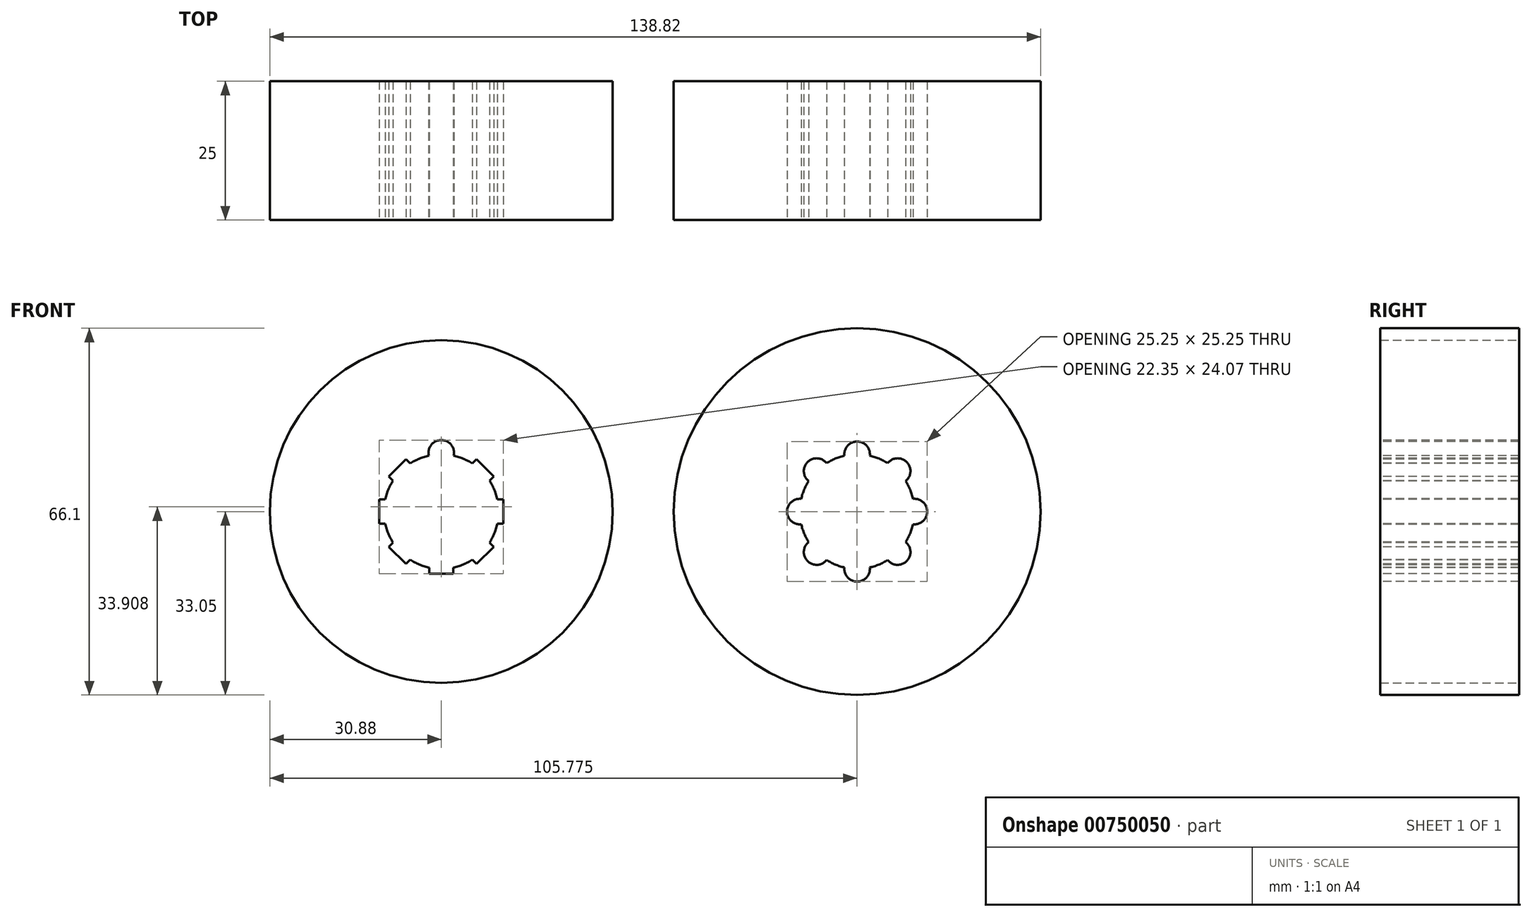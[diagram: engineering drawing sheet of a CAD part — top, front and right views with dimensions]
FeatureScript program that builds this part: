
annotation { "Feature Type Name" : "Feature", "Feature Type Description" : "" }
export const myFeature = defineFeature(function(context is Context, id is Id, definition is map)
    precondition{}
    {
        {
            var Q0;
            Q0=qCreatedBy(makeId("Front.planeOp"),FACE);
            var sketch = newSketch(context, id + "F0", { "sketchPlane" : qUnion([Q0])});
            skCircle(sketch, "E0", {"center": v(0, 0) * mm, "radius": 30.88 * mm});
            skSolve(sketch);
        }
        {
            var Q0;
            Q0 = qSketchRegion(id + "F0", true);
            extrude(context, id + "F1", {"entities" : qUnion([Q0]), "depth" : 25 * mm, "offsetDistance" : 25 * mm});
        }
        {
            var Q0;
            Q0=makeQuery(id+"F1.opExtrude","CAP_FACE",FACE,{"disambiguationData":[OSD([sQuery(id+"F0.wireOp",EDGE,"E0")])],"isStart":false});
            var sketch = newSketch(context, id + "F2", { "sketchPlane" : qUnion([Q0])});
            skCircle(sketch, "E1", {"center": v(0, 0) * mm, "radius": 11.18 * mm, "construction": true});
            skArc(sketch, "E2", {"start": v(-8.68, 5.6) * mm, "mid": v(-9.54, 3.95) * mm, "end": v(-10.1, 2.18) * mm});
            skLineSegment(sketch, "E3", {"start": v(0, 0) * mm, "end": v(0, 21.23) * mm, "construction": true});
            skLineSegment(sketch, "E4", {"start": v(0, 11.18) * mm, "end": v(2.18, 11.18) * mm, "construction": true});
            skLineSegment(sketch, "E5", {"start": v(2.18, 11.18) * mm, "end": v(-2.18, 11.18) * mm});
            skLineSegment(sketch, "E6", {"start": v(-2.18, 11.18) * mm, "end": v(-2.18, 10.1) * mm});
            skLineSegment(sketch, "E7", {"start": v(2.18, 11.18) * mm, "end": v(2.18, 10.1) * mm});
            skLineSegment(sketch, "E8.1.0", {"start": v(-9.44, 6.36) * mm, "end": v(-8.68, 5.6) * mm});
            skLineSegment(sketch, "E8.1.1", {"start": v(-6.36, 9.44) * mm, "end": v(-9.44, 6.36) * mm});
            skLineSegment(sketch, "E8.1.2", {"start": v(-6.36, 9.44) * mm, "end": v(-5.6, 8.68) * mm});
            skLineSegment(sketch, "E8.2.0", {"start": v(-11.18, -2.18) * mm, "end": v(-10.1, -2.18) * mm});
            skLineSegment(sketch, "E8.2.1", {"start": v(-11.18, 2.18) * mm, "end": v(-11.18, -2.18) * mm});
            skLineSegment(sketch, "E8.2.2", {"start": v(-11.18, 2.18) * mm, "end": v(-10.1, 2.18) * mm});
            skLineSegment(sketch, "E8.3.0", {"start": v(-6.36, -9.44) * mm, "end": v(-5.6, -8.68) * mm});
            skLineSegment(sketch, "E8.3.1", {"start": v(-9.44, -6.36) * mm, "end": v(-6.36, -9.44) * mm});
            skLineSegment(sketch, "E8.3.2", {"start": v(-9.44, -6.36) * mm, "end": v(-8.68, -5.6) * mm});
            skLineSegment(sketch, "E8.4.0", {"start": v(2.18, -11.18) * mm, "end": v(2.18, -10.1) * mm});
            skLineSegment(sketch, "E8.4.1", {"start": v(-2.18, -11.18) * mm, "end": v(2.18, -11.18) * mm});
            skLineSegment(sketch, "E8.4.2", {"start": v(-2.18, -11.18) * mm, "end": v(-2.18, -10.1) * mm});
            skLineSegment(sketch, "E8.5.0", {"start": v(9.44, -6.36) * mm, "end": v(8.68, -5.6) * mm});
            skLineSegment(sketch, "E8.5.1", {"start": v(6.36, -9.44) * mm, "end": v(9.44, -6.36) * mm});
            skLineSegment(sketch, "E8.5.2", {"start": v(6.36, -9.44) * mm, "end": v(5.6, -8.68) * mm});
            skLineSegment(sketch, "E8.6.0", {"start": v(11.18, 2.18) * mm, "end": v(10.1, 2.18) * mm});
            skLineSegment(sketch, "E8.6.1", {"start": v(11.18, -2.18) * mm, "end": v(11.18, 2.18) * mm});
            skLineSegment(sketch, "E8.6.2", {"start": v(11.18, -2.18) * mm, "end": v(10.1, -2.18) * mm});
            skLineSegment(sketch, "E8.7.0", {"start": v(6.36, 9.44) * mm, "end": v(5.6, 8.68) * mm});
            skLineSegment(sketch, "E8.7.1", {"start": v(9.44, 6.36) * mm, "end": v(6.36, 9.44) * mm});
            skLineSegment(sketch, "E8.7.2", {"start": v(9.44, 6.36) * mm, "end": v(8.68, 5.6) * mm});
            skArc(sketch, "E9.trimOffspring", {"start": v(-2.18, 10.1) * mm, "mid": v(-3.95, 9.54) * mm, "end": v(-5.6, 8.68) * mm});
            skArc(sketch, "E10.trimOffspring", {"start": v(5.6, 8.68) * mm, "mid": v(3.95, 9.54) * mm, "end": v(2.18, 10.1) * mm});
            skArc(sketch, "E11.trimOffspring", {"start": v(10.1, 2.18) * mm, "mid": v(9.54, 3.95) * mm, "end": v(8.68, 5.6) * mm});
            skArc(sketch, "E12.trimOffspring", {"start": v(8.68, -5.6) * mm, "mid": v(9.54, -3.95) * mm, "end": v(10.1, -2.18) * mm});
            skArc(sketch, "E13.trimOffspring", {"start": v(2.18, -10.1) * mm, "mid": v(3.95, -9.54) * mm, "end": v(5.6, -8.68) * mm});
            skArc(sketch, "E14.trimOffspring", {"start": v(-5.6, -8.68) * mm, "mid": v(-3.95, -9.54) * mm, "end": v(-2.18, -10.1) * mm});
            skArc(sketch, "E15.trimOffspring", {"start": v(-10.1, -2.18) * mm, "mid": v(-9.54, -3.95) * mm, "end": v(-8.68, -5.6) * mm});
            skSolve(sketch);
        }
        {
            var Q0;
            Q0 = qSketchRegion(id + "F2", true);
            extrude(context, id + "F3", {"entities" : qUnion([Q0]), "operationType" : NewBodyOperationType.REMOVE, "oppositeDirection" : true, "depth" : 25 * mm, "offsetDistance" : 25 * mm});
        }
        {
            var Q0;
            Q0=makeQuery(id+"F1.opExtrude","CAP_FACE",FACE,{"disambiguationData":[OSD([sQuery(id+"F0.wireOp",EDGE,"E0")])],"isStart":false});
            var sketch = newSketch(context, id + "F4", { "sketchPlane" : qUnion([Q0])});
            skCircle(sketch, "E16", {"center": v(0, 10.6) * mm, "radius": 2.3 * mm});
            skCircle(sketch, "E17", {"center": v(0, 0) * mm, "radius": 10.6 * mm, "construction": true});
            skSolve(sketch);
        }
        {
            var Q0;
            Q0 = qSketchRegion(id + "F4", true);
            extrude(context, id + "F5", {"entities" : qUnion([Q0]), "operationType" : NewBodyOperationType.REMOVE, "oppositeDirection" : true, "depth" : 25 * mm, "offsetDistance" : 25 * mm});
        }
        {
            var Q0;
            Q0=qCreatedBy(makeId("Front.planeOp"),FACE);
            var sketch = newSketch(context, id + "F6", { "sketchPlane" : qUnion([Q0])});
            skCircle(sketch, "E18", {"center": v(74.9, 0) * mm, "radius": 33.05 * mm});
            skSolve(sketch);
        }
        {
            var Q0;
            Q0 = qSketchRegion(id + "F6", true);
            extrude(context, id + "F7", {"entities" : qUnion([Q0]), "depth" : 25 * mm, "offsetDistance" : 25 * mm});
        }
        {
            var Q0;
            Q0=makeQuery(id+"F7.opExtrude","CAP_FACE",FACE,{"disambiguationData":[OSD([sQuery(id+"F6.wireOp",EDGE,"E18")])],"isStart":false});
            var sketch = newSketch(context, id + "F8", { "sketchPlane" : qUnion([Q0])});
            skArc(sketch, "E19", {"start": v(66.16, 5.5) * mm, "mid": v(65.36, 3.95) * mm, "end": v(64.83, 2.29) * mm});
            skLineSegment(sketch, "E20", {"start": v(74.9, 0) * mm, "end": v(74.9, 14.64) * mm, "construction": true});
            skArc(sketch, "E21", {"start": v(77.18, 10.07) * mm, "mid": v(74.9, 12.62) * mm, "end": v(72.6, 10.07) * mm});
            skArc(sketch, "E22.1.0", {"start": v(69.4, 8.74) * mm, "mid": v(65.97, 8.93) * mm, "end": v(66.16, 5.5) * mm});
            skArc(sketch, "E22.2.0", {"start": v(64.83, 2.29) * mm, "mid": v(62.27, 0) * mm, "end": v(64.83, -2.29) * mm});
            skArc(sketch, "E22.3.0", {"start": v(66.16, -5.5) * mm, "mid": v(65.97, -8.93) * mm, "end": v(69.4, -8.74) * mm});
            skArc(sketch, "E22.4.0", {"start": v(72.6, -10.07) * mm, "mid": v(74.9, -12.62) * mm, "end": v(77.18, -10.07) * mm});
            skArc(sketch, "E22.5.0", {"start": v(80.4, -8.74) * mm, "mid": v(83.82, -8.93) * mm, "end": v(83.63, -5.5) * mm});
            skArc(sketch, "E22.6.0", {"start": v(84.96, -2.29) * mm, "mid": v(87.52, 0) * mm, "end": v(84.96, 2.29) * mm});
            skArc(sketch, "E22.7.0", {"start": v(83.63, 5.5) * mm, "mid": v(83.82, 8.93) * mm, "end": v(80.4, 8.74) * mm});
            skLineSegment(sketch, "E22.anchor1", {"start": v(74.9, 0) * mm, "end": v(74.9, 10.32) * mm, "construction": true});
            skLineSegment(sketch, "E22.anchor2", {"start": v(74.9, 0) * mm, "end": v(82.2, 7.3) * mm, "construction": true});
            skArc(sketch, "E23.trimOffspring", {"start": v(72.6, 10.07) * mm, "mid": v(70.94, 9.54) * mm, "end": v(69.4, 8.74) * mm});
            skArc(sketch, "E24.trimOffspring", {"start": v(80.4, 8.74) * mm, "mid": v(78.85, 9.54) * mm, "end": v(77.18, 10.07) * mm});
            skArc(sketch, "E25.trimOffspring", {"start": v(84.96, 2.29) * mm, "mid": v(84.43, 3.95) * mm, "end": v(83.63, 5.5) * mm});
            skArc(sketch, "E26.trimOffspring", {"start": v(83.63, -5.5) * mm, "mid": v(84.43, -3.95) * mm, "end": v(84.96, -2.29) * mm});
            skArc(sketch, "E27.trimOffspring", {"start": v(77.18, -10.07) * mm, "mid": v(78.85, -9.54) * mm, "end": v(80.4, -8.74) * mm});
            skArc(sketch, "E28.trimOffspring", {"start": v(69.4, -8.74) * mm, "mid": v(70.94, -9.54) * mm, "end": v(72.6, -10.07) * mm});
            skArc(sketch, "E29.trimOffspring", {"start": v(64.83, -2.29) * mm, "mid": v(65.36, -3.95) * mm, "end": v(66.16, -5.5) * mm});
            skSolve(sketch);
        }
        {
            var Q0;
            Q0 = qSketchRegion(id + "F8", true);
            extrude(context, id + "F9", {"entities" : qUnion([Q0]), "operationType" : NewBodyOperationType.REMOVE, "oppositeDirection" : true, "depth" : 25 * mm, "offsetDistance" : 25 * mm});
        }
    });
